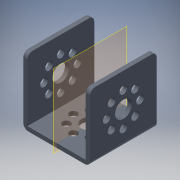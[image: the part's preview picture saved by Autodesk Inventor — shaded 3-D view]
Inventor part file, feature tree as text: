
AUTODESK INVENTOR PART (.ipt)
format: ipt  version: 2019 (Build 230136000, 136)  size: 217,088 bytes
history: native  units: in
note: dims shown in document units (in); Inventor stores cm internally (conversion verified against a paired STEP export)
features: other x23, plane x1, imported_body x1
ambient origin geometry x8: Origin, YZ Plane, XZ Plane, XY Plane, X Axis, Y Axis, Z Axis, Center Point
bodies: Body1 (feature_tree)
feature tree (25):
  other  "tetrix_739065_2012"
  other  "tetrix_739065_20121"
  other  "A_1"
  other  "A_18"
  other  "A_10"
  other  "A_11"
  other  "A_12"
  other  "A_13"
  other  "A_14"
  other  "A_15"
  other  "A_16"
  other  "A_17"
  other  "A_19"
  other  "A_20"
  other  "A_21"
  other  "A_22"
  other  "A_23"
  other  "A_24"
  other  "A_25"
  other  "A_26"
  other  "FRONT"
  other  "TOP"
  other  "RIGHT"
  plane  "Work Plane4"
  imported_body  "Base1"
